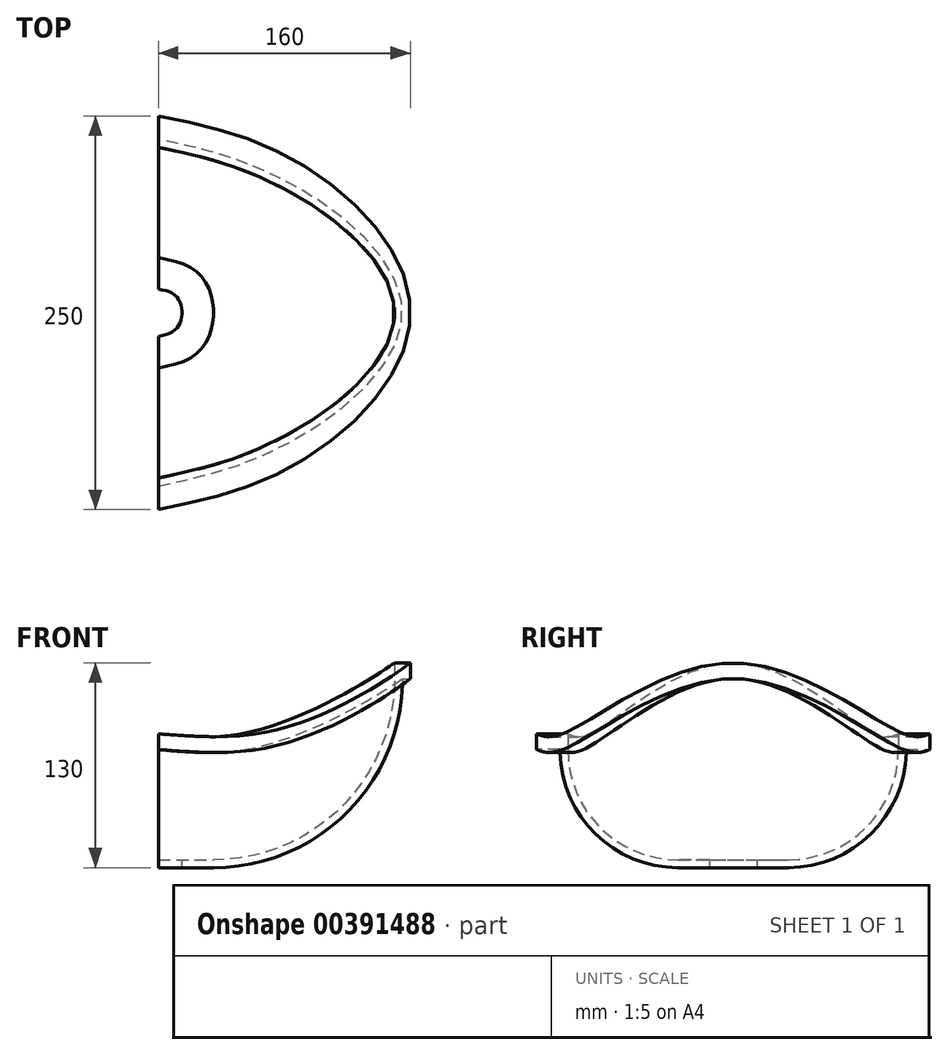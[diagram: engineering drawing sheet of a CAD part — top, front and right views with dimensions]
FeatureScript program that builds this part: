
annotation { "Feature Type Name" : "Feature", "Feature Type Description" : "" }
export const myFeature = defineFeature(function(context is Context, id is Id, definition is map)
    precondition{}
    {
        {
            var Q0;
            Q0=qCreatedBy(makeId("Front.planeOp"),FACE);
            var sketch = newSketch(context, id + "F0", { "sketchPlane" : qUnion([Q0])});
            skLineSegment(sketch, "E0.bottom", {"start": v(15, 5) * mm, "end": v(35, 5) * mm});
            skLineSegment(sketch, "E0.top", {"start": v(15, 0) * mm, "end": v(35, 0) * mm});
            skLineSegment(sketch, "E0.left", {"start": v(15, 5) * mm, "end": v(15, 0) * mm});
            skLineSegment(sketch, "E0.right", {"start": v(35, 5) * mm, "end": v(35, 0) * mm, "construction": true});
            skLineSegment(sketch, "E1.bottom", {"start": v(150, 130) * mm, "end": v(160, 130) * mm});
            skLineSegment(sketch, "E1.top", {"start": v(155, 120) * mm, "end": v(160, 120) * mm});
            skLineSegment(sketch, "E1.left", {"start": v(150, 130) * mm, "end": v(150, 120) * mm});
            skLineSegment(sketch, "E1.right", {"start": v(160, 130) * mm, "end": v(160, 120) * mm});
            skArc(sketch, "E2", {"start": v(35, 0) * mm, "mid": v(119.85, 35.15) * mm, "end": v(155, 120) * mm});
            skArc(sketch, "E3", {"start": v(35, 5) * mm, "mid": v(116.32, 38.68) * mm, "end": v(150, 120) * mm});
            skLineSegment(sketch, "E4", {"start": v(0, 0) * mm, "end": v(0, 50) * mm, "construction": true});
            skSolve(sketch);
        }
        {
            var Q0;
            Q0=sQuery(id+"F0.wireOp",EDGE,"E4");
            cPlane(context, id + "F1", {"entities" : qUnion([Q0]), "cplaneType" : CPlaneType.LINE_ANGLE, "offset" : 25 * mm, "angle" : 30 * degree, "oppositeDirection" : true, "width" : 150 * mm, "height" : 150 * mm});
        }
        {
            var Q0;
            Q0=qCreatedBy(id+"F1.planeOp",FACE);
            var sketch = newSketch(context, id + "F2", { "sketchPlane" : qUnion([Q0])});
            skLineSegment(sketch, "E5.bottom", {"start": v(15, 5) * mm, "end": v(35, 5) * mm});
            skLineSegment(sketch, "E5.top", {"start": v(15, 0) * mm, "end": v(35, 0) * mm});
            skLineSegment(sketch, "E5.left", {"start": v(15, 5) * mm, "end": v(15, 0) * mm});
            skLineSegment(sketch, "E5.right", {"start": v(35, 5) * mm, "end": v(35, 0) * mm, "construction": true});
            skLineSegment(sketch, "E6.bottom", {"start": v(105, 85) * mm, "end": v(125, 85) * mm});
            skLineSegment(sketch, "E6.top", {"start": v(110, 75) * mm, "end": v(125, 75) * mm});
            skLineSegment(sketch, "E6.left", {"start": v(105, 85) * mm, "end": v(105, 75) * mm});
            skLineSegment(sketch, "E6.right", {"start": v(125, 85) * mm, "end": v(125, 75) * mm});
            skArc(sketch, "E7", {"start": v(35, 0) * mm, "mid": v(88.03, 21.97) * mm, "end": v(110, 75) * mm});
            skArc(sketch, "E8", {"start": v(35, 5) * mm, "mid": v(84.5, 25.5) * mm, "end": v(105, 75) * mm});
            skLineSegment(sketch, "E9", {"start": v(0, 0) * mm, "end": v(0, 50) * mm, "construction": true});
            skSolve(sketch);
        }
        {
            var Q0;
            Q0=sQuery(id+"F2.wireOp",EDGE,"E9");
            cPlane(context, id + "F3", {"entities" : qUnion([Q0]), "cplaneType" : CPlaneType.LINE_ANGLE, "offset" : 25 * mm, "angle" : 150 * degree, "oppositeDirection" : true, "width" : 150 * mm, "height" : 150 * mm});
        }
        {
            var Q0;
            Q0=qCreatedBy(id+"F3.planeOp",FACE);
            var sketch = newSketch(context, id + "F4", { "sketchPlane" : qUnion([Q0])});
            skLineSegment(sketch, "E10.bottom", {"start": v(15, 5) * mm, "end": v(35, 5) * mm});
            skLineSegment(sketch, "E10.top", {"start": v(15, 0) * mm, "end": v(35, 0) * mm});
            skLineSegment(sketch, "E10.left", {"start": v(15, 5) * mm, "end": v(15, 0) * mm});
            skLineSegment(sketch, "E10.right", {"start": v(35, 5) * mm, "end": v(35, 0) * mm, "construction": true});
            skLineSegment(sketch, "E11.bottom", {"start": v(105, 85) * mm, "end": v(125, 85) * mm});
            skLineSegment(sketch, "E11.top", {"start": v(110, 75) * mm, "end": v(125, 75) * mm});
            skLineSegment(sketch, "E11.left", {"start": v(105, 85) * mm, "end": v(105, 75) * mm});
            skLineSegment(sketch, "E11.right", {"start": v(125, 85) * mm, "end": v(125, 75) * mm});
            skArc(sketch, "E12", {"start": v(35, 0) * mm, "mid": v(88.03, 21.97) * mm, "end": v(110, 75) * mm});
            skArc(sketch, "E13", {"start": v(35, 5) * mm, "mid": v(84.5, 25.5) * mm, "end": v(105, 75) * mm});
            skLineSegment(sketch, "E14", {"start": v(0, 0) * mm, "end": v(0, 50) * mm, "construction": true});
            skSolve(sketch);
        }
        {
            var Q0;
            Q0=qCreatedBy(makeId("Right.planeOp"),FACE);
            var sketch = newSketch(context, id + "F5", { "sketchPlane" : qUnion([Q0])});
            skLineSegment(sketch, "E15.bottom", {"start": v(15, 5) * mm, "end": v(35, 5) * mm});
            skLineSegment(sketch, "E15.top", {"start": v(15, 0) * mm, "end": v(35, 0) * mm});
            skLineSegment(sketch, "E15.left", {"start": v(15, 5) * mm, "end": v(15, 0) * mm});
            skLineSegment(sketch, "E15.right", {"start": v(35, 5) * mm, "end": v(35, 0) * mm, "construction": true});
            skLineSegment(sketch, "E16.bottom", {"start": v(105, 85) * mm, "end": v(125, 85) * mm});
            skLineSegment(sketch, "E16.top", {"start": v(110, 75) * mm, "end": v(125, 75) * mm});
            skLineSegment(sketch, "E16.left", {"start": v(105, 85) * mm, "end": v(105, 75) * mm});
            skLineSegment(sketch, "E16.right", {"start": v(125, 85) * mm, "end": v(125, 75) * mm});
            skArc(sketch, "E17", {"start": v(35, 0) * mm, "mid": v(88.03, 21.97) * mm, "end": v(110, 75) * mm});
            skArc(sketch, "E18", {"start": v(35, 5) * mm, "mid": v(84.5, 25.5) * mm, "end": v(105, 75) * mm});
            skLineSegment(sketch, "E19", {"start": v(0, 0) * mm, "end": v(0, 50) * mm, "construction": true});
            skSolve(sketch);
        }
        {
            var Q0;
            Q0=sQuery(id+"F5.wireOp",EDGE,"E19");
            cPlane(context, id + "F6", {"entities" : qUnion([Q0]), "cplaneType" : CPlaneType.LINE_ANGLE, "offset" : 25 * mm, "angle" : 180 * degree, "width" : 150 * mm, "height" : 150 * mm});
        }
        {
            var Q0;
            Q0=qCreatedBy(id+"F6.planeOp",FACE);
            var sketch = newSketch(context, id + "F7", { "sketchPlane" : qUnion([Q0])});
            skLineSegment(sketch, "E20.bottom", {"start": v(15, 5) * mm, "end": v(35, 5) * mm});
            skLineSegment(sketch, "E20.top", {"start": v(15, 0) * mm, "end": v(35, 0) * mm});
            skLineSegment(sketch, "E20.left", {"start": v(15, 5) * mm, "end": v(15, 0) * mm});
            skLineSegment(sketch, "E20.right", {"start": v(35, 5) * mm, "end": v(35, 0) * mm, "construction": true});
            skLineSegment(sketch, "E21.bottom", {"start": v(105, 85) * mm, "end": v(125, 85) * mm});
            skLineSegment(sketch, "E21.top", {"start": v(110, 75) * mm, "end": v(125, 75) * mm});
            skLineSegment(sketch, "E21.left", {"start": v(105, 85) * mm, "end": v(105, 75) * mm});
            skLineSegment(sketch, "E21.right", {"start": v(125, 85) * mm, "end": v(125, 75) * mm});
            skArc(sketch, "E22", {"start": v(35, 0) * mm, "mid": v(88.03, 21.97) * mm, "end": v(110, 75) * mm});
            skArc(sketch, "E23", {"start": v(35, 5) * mm, "mid": v(84.5, 25.5) * mm, "end": v(105, 75) * mm});
            skLineSegment(sketch, "E24", {"start": v(0, 0) * mm, "end": v(0, 50) * mm, "construction": true});
            skSolve(sketch);
        }
        {
            var Q0;
            Q0 = qSketchRegion(id + "F7", true);
            var Q1;
            Q1 = qSketchRegion(id + "F4", true);
            var Q2;
            Q2 = qSketchRegion(id + "F0", true);
            var Q3;
            Q3 = qSketchRegion(id + "F2", true);
            var Q4;
            Q4 = qSketchRegion(id + "F5", true);
            loft(context, id + "F8", {"sheetProfilesArray" : [{ "sheetProfileEntities" : qUnion([Q0]) }, { "sheetProfileEntities" : qUnion([Q1]) }, { "sheetProfileEntities" : qUnion([Q2]) }, { "sheetProfileEntities" : qUnion([Q3]) }, { "sheetProfileEntities" : qUnion([Q4]) }]});
        }
    });
